# Revit family: QF_NuovAIR_P5.1----
name_source: partatom
category: Specialty Equipment
units: mm (PartAtom-declared; Revit-internal decimal feet)

## family parameters
Always vertical = Yes
Cut with Voids When Loaded = No
Part Type = Normal
Room Calculation Point = No
Round Connector Dimension = Use Diameter
Shared = No
Work Plane-Based = No

## types (4) — shared parameters
Accessory = No
CE Approved = Yes
Conn Plug = Cable with Shuko plug
D15 = 15 mm  [stored 0.0492126 ft]
Depth Actual = 853 mm  [stored 2.79856 ft]
Description = Blast Chiller, 4-6 tray GN1/1 - 60x40
Direct Waste Size = 0 mm
DoorH = 545 mm  [stored 1.78806 ft]
Elec Connection Height = 355 mm
Electric power = 1700000 W
Foodservice Equipment Identifier = Yes
Height Actual = 970 mm  [stored 3.18241 ft]
Identify Quantity as Lot = No
Item Number = P5.1
Keynote = 0
Legs_R1 = 30 mm  [stored 0.0984252 ft]
Legs_R2 = 25 mm  [stored 0.082021 ft]
Length Actual = 820 mm  [stored 2.69029 ft]
Main switch integrated = No
Manufacturer = NUOVAIR
Mat_Case = QF_Stainless-Brushed
Mat_Clearance = QF_Clearance
Mat_Handle = QF_Stainless-Brushed
Mat_Legs = QF_Stainless-Brushed
Model = P5.1
Number of Poles = 1
Phase = 1
Potential Equalisation = Yes
Refrigerant Compressor Remote = No
Refrigerant Type = R452a
Refrigeration Liquid Line Size = 0 mm
Refrigeration Suction Line Size = 0 mm
URL Cutsheet = P5.1-en.pdf
URL Manufacturer = https://www.nuovair.com
Volt Free Conn = No
Weight = 115.00 kg
zero-valued in all types: Direct Waste Connection Height

## per-type parameters (varying)
| type | Cycle | FL Amps | RH | Volts |
| P5.1_LH_220V 50A | 50 Hz | 8 A | No | 220 V |
| P5.1_RH_220V 50A | 50 Hz | 8 A | Yes | 220 V |
| P5.1_LH_208V 60A | 60 Hz | 10 A | No | 208 V |
| P5.1_RH_208V 60A | 60 Hz | 10 A | Yes | 208 V |

note: [stored X ft] marks values corroborated as IEEE doubles in the binary element streams (Revit-internal decimal feet)

## geometry (parser evidence)
native form markers: Sweep x11
no freeform markers — native parametric forms only
